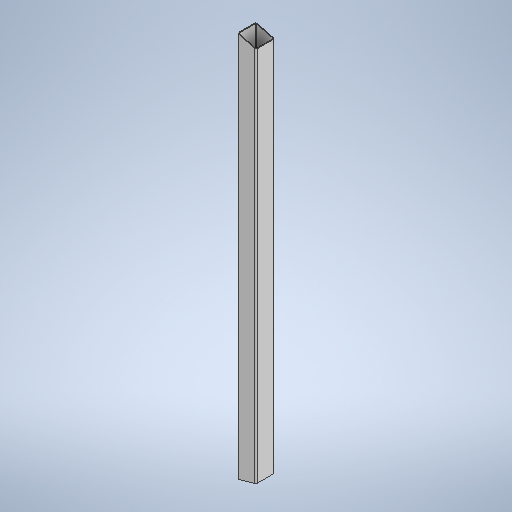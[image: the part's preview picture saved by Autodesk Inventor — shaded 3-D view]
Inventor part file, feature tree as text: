
AUTODESK INVENTOR PART (.ipt)
format: ipt  version: 2025 (Build 290162010, 162A)  size: 292,864 bytes
history: native  units: mm
features: extrude x2, sketch x2, mirror x1
ambient origin geometry x8: Origin, YZ Plane, XZ Plane, XY Plane, X Axis, Y Axis, Z Axis, Center Point
bodies: Solid1 (feature_tree)
feature tree (5):
  extrude  "Extrusion1"  Depth=8.0mm
  extrude  "Extrusion2"  Depth=120.0mm
  mirror  "Mirror1"
  sketch  "Sketch1"  dims[d0=8.0mm d1=120.0mm d2=120.0mm d3=4.0mm d6=8.0mm]
  sketch  "Sketch2"  dims[d7=120.0mm d8=120.0mm d9=4.0mm d14=2500.0mm d15=0.0mm d16=15.0deg d17=2000.0mm d18=0.0mm]
